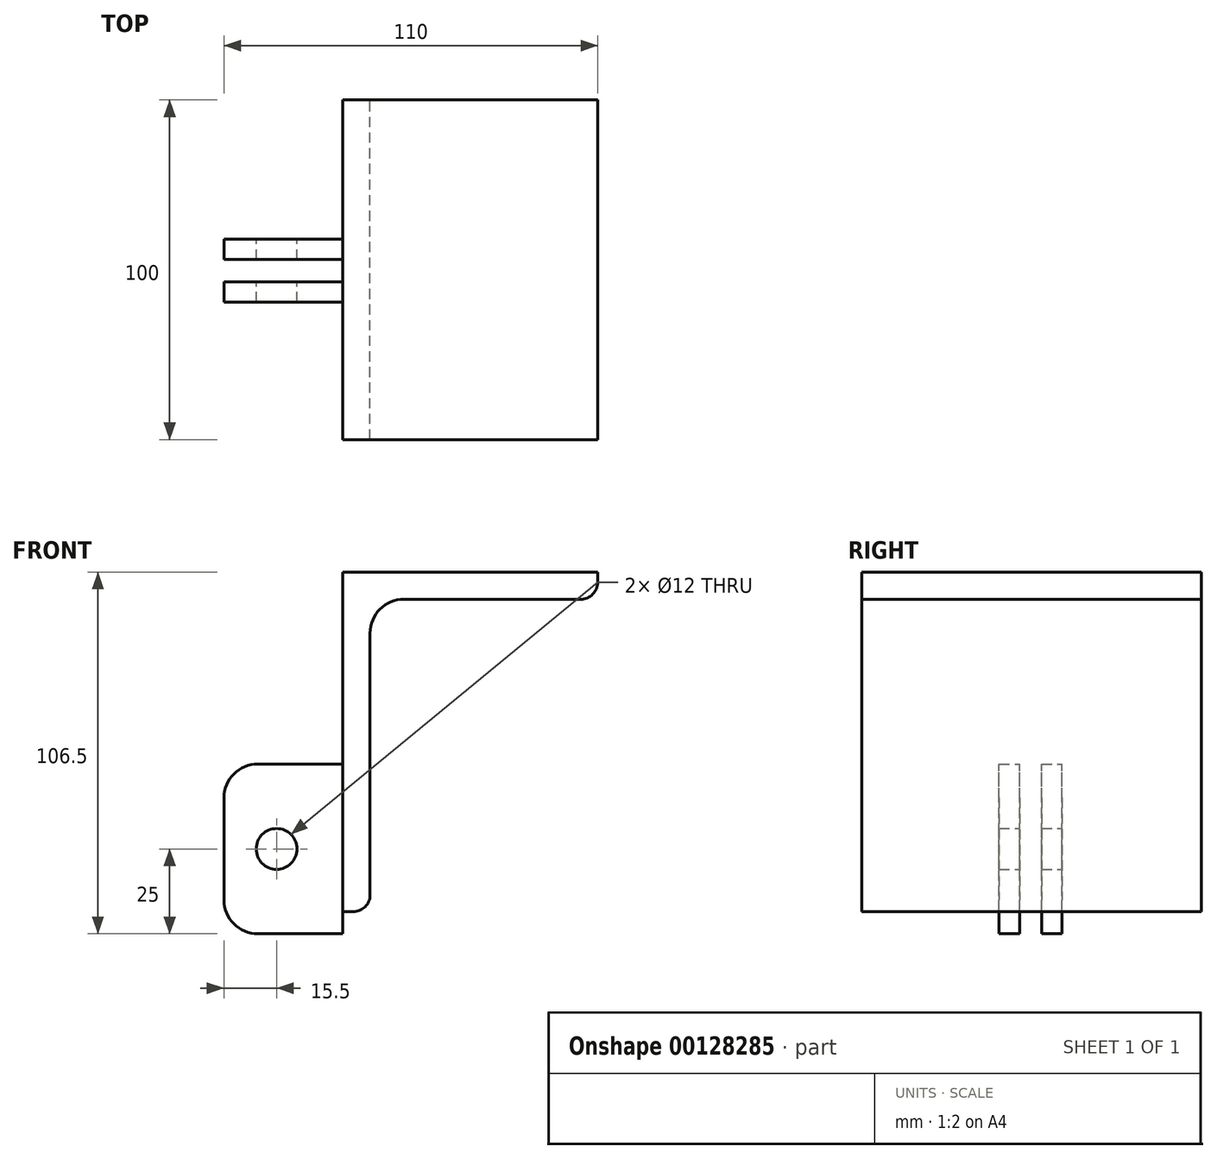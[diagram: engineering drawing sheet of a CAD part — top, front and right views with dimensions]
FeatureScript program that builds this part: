
annotation { "Feature Type Name" : "Feature", "Feature Type Description" : "" }
export const myFeature = defineFeature(function(context is Context, id is Id, definition is map)
    precondition{}
    {
        {
            var Q0;
            Q0=qCreatedBy(makeId("Front.planeOp"),FACE);
            var sketch = newSketch(context, id + "F0", { "sketchPlane" : qUnion([Q0])});
            skLineSegment(sketch, "E0", {"start": v(-75, 0) * mm, "end": v(0, 0) * mm});
            skLineSegment(sketch, "E1", {"start": v(0, 0) * mm, "end": v(0, -100) * mm});
            skLineSegment(sketch, "E2", {"start": v(0, -100) * mm, "end": v(-3, -100) * mm});
            skLineSegment(sketch, "E3", {"start": v(-8, -95) * mm, "end": v(-8, -18) * mm});
            skLineSegment(sketch, "E4", {"start": v(-18, -8) * mm, "end": v(-70, -8) * mm});
            skLineSegment(sketch, "E5", {"start": v(-75, -3) * mm, "end": v(-75, 0) * mm});
            skPoint(sketch, "E6.visualSharp", {"position": v(-8, -8) * mm});
            skArc(sketch, "E6.filletArc", {"start": v(-8, -18) * mm, "mid": v(-10.93, -10.93) * mm, "end": v(-18, -8) * mm});
            skPoint(sketch, "E7.visualSharp", {"position": v(-75, -8) * mm});
            skArc(sketch, "E7.filletArc", {"start": v(-75, -3) * mm, "mid": v(-73.54, -6.54) * mm, "end": v(-70, -8) * mm});
            skPoint(sketch, "E8.visualSharp", {"position": v(-8, -100) * mm});
            skArc(sketch, "E8.filletArc", {"start": v(-8, -95) * mm, "mid": v(-6.54, -98.54) * mm, "end": v(-3, -100) * mm});
            skSolve(sketch);
        }
        {
            var Q0;
            Q0 = qSketchRegion(id + "F0", true);
            extrude(context, id + "F1", {"entities" : qUnion([Q0]), "oppositeDirection" : true, "depth" : 100 * mm});
        }
        {
            var Q0;
            Q0=qCreatedBy(makeId("Front.planeOp"),FACE);
            cPlane(context, id + "F2", {"entities" : qUnion([Q0]), "cplaneType" : CPlaneType.OFFSET, "offset" : 41 * mm, "oppositeDirection" : true, "width" : 150 * mm, "height" : 150 * mm});
        }
        {
            var Q0;
            Q0=qCreatedBy(id+"F2.planeOp",FACE);
            var sketch = newSketch(context, id + "F3", { "sketchPlane" : qUnion([Q0])});
            skLineSegment(sketch, "E9", {"start": v(0, -56.5) * mm, "end": v(25, -56.5) * mm});
            skLineSegment(sketch, "E10", {"start": v(35, -66.5) * mm, "end": v(35, -96.5) * mm});
            skLineSegment(sketch, "E11", {"start": v(25, -106.5) * mm, "end": v(0, -106.5) * mm});
            skLineSegment(sketch, "E12", {"start": v(0, -106.5) * mm, "end": v(0, -56.5) * mm});
            skCircle(sketch, "E13", {"center": v(19.5, -81.5) * mm, "radius": 6 * mm});
            skPoint(sketch, "E14.visualSharp", {"position": v(35, -56.5) * mm});
            skArc(sketch, "E14.filletArc", {"start": v(35, -66.5) * mm, "mid": v(32.07, -59.43) * mm, "end": v(25, -56.5) * mm});
            skPoint(sketch, "E15.visualSharp", {"position": v(35, -106.5) * mm});
            skArc(sketch, "E15.filletArc", {"start": v(25, -106.5) * mm, "mid": v(32.07, -103.57) * mm, "end": v(35, -96.5) * mm});
            skSolve(sketch);
        }
        {
            var Q0;
            Q0 = qSketchRegion(id + "F3", true);
            extrude(context, id + "F4", {"entities" : qUnion([Q0]), "operationType" : NewBodyOperationType.ADD, "oppositeDirection" : true, "depth" : 6 * mm});
        }
        {
            var Q0;
            Q0=qCreatedBy(id+"F2.planeOp",FACE);
            cPlane(context, id + "F5", {"entities" : qUnion([Q0]), "cplaneType" : CPlaneType.OFFSET, "offset" : 12.5 * mm, "oppositeDirection" : true, "width" : 150 * mm, "height" : 150 * mm});
        }
        {
            var Q0;
            Q0=qCreatedBy(id+"F5.planeOp",FACE);
            var sketch = newSketch(context, id + "F6", { "sketchPlane" : qUnion([Q0])});
            skLineSegment(sketch, "E16", {"start": v(0, -56.5) * mm, "end": v(25, -56.5) * mm});
            skLineSegment(sketch, "E17", {"start": v(35, -66.5) * mm, "end": v(35, -96.5) * mm});
            skLineSegment(sketch, "E18", {"start": v(25, -106.5) * mm, "end": v(0, -106.5) * mm});
            skLineSegment(sketch, "E19", {"start": v(0, -106.5) * mm, "end": v(0, -56.5) * mm});
            skCircle(sketch, "E20", {"center": v(19.5, -81.5) * mm, "radius": 6 * mm});
            skPoint(sketch, "E21.visualSharp", {"position": v(35, -56.5) * mm});
            skArc(sketch, "E21.filletArc", {"start": v(35, -66.5) * mm, "mid": v(32.07, -59.43) * mm, "end": v(25, -56.5) * mm});
            skPoint(sketch, "E22.visualSharp", {"position": v(35, -106.5) * mm});
            skArc(sketch, "E22.filletArc", {"start": v(25, -106.5) * mm, "mid": v(32.07, -103.57) * mm, "end": v(35, -96.5) * mm});
            skSolve(sketch);
        }
        {
            var Q0;
            Q0 = qSketchRegion(id + "F6", true);
            extrude(context, id + "F7", {"entities" : qUnion([Q0]), "operationType" : NewBodyOperationType.ADD, "oppositeDirection" : true, "depth" : 6 * mm});
        }
        {
            var Q0;
            Q0=makeQuery(id+"F1.opExtrude","SWEPT_BODY",BODY,{"disambiguationData":[OSD([sQuery(id+"F0.wireOp",EDGE,"E0"),sQuery(id+"F0.wireOp",EDGE,"E1"),sQuery(id+"F0.wireOp",EDGE,"E2"),sQuery(id+"F0.wireOp",EDGE,"E3"),sQuery(id+"F0.wireOp",EDGE,"E4"),sQuery(id+"F0.wireOp",EDGE,"E5"),sQuery(id+"F0.wireOp",EDGE,"E6.filletArc"),sQuery(id+"F0.wireOp",EDGE,"E7.filletArc"),sQuery(id+"F0.wireOp",EDGE,"E8.filletArc")])]});
            var Q1;
            Q1=makeQuery(id+"F1.opExtrude","CAP_EDGE",EDGE,{"disambiguationData":[OSD([sQuery(id+"F0.wireOp",EDGE,"E1")])],"isStart":true});
            transform(context, id + "F8", {"entities" : qUnion([Q0]), "transformType" : TransformType.ROTATION, "transformAxis" : qUnion([Q1]), "angle" : 180 * degree, "makeCopy" : false});
        }
    });
